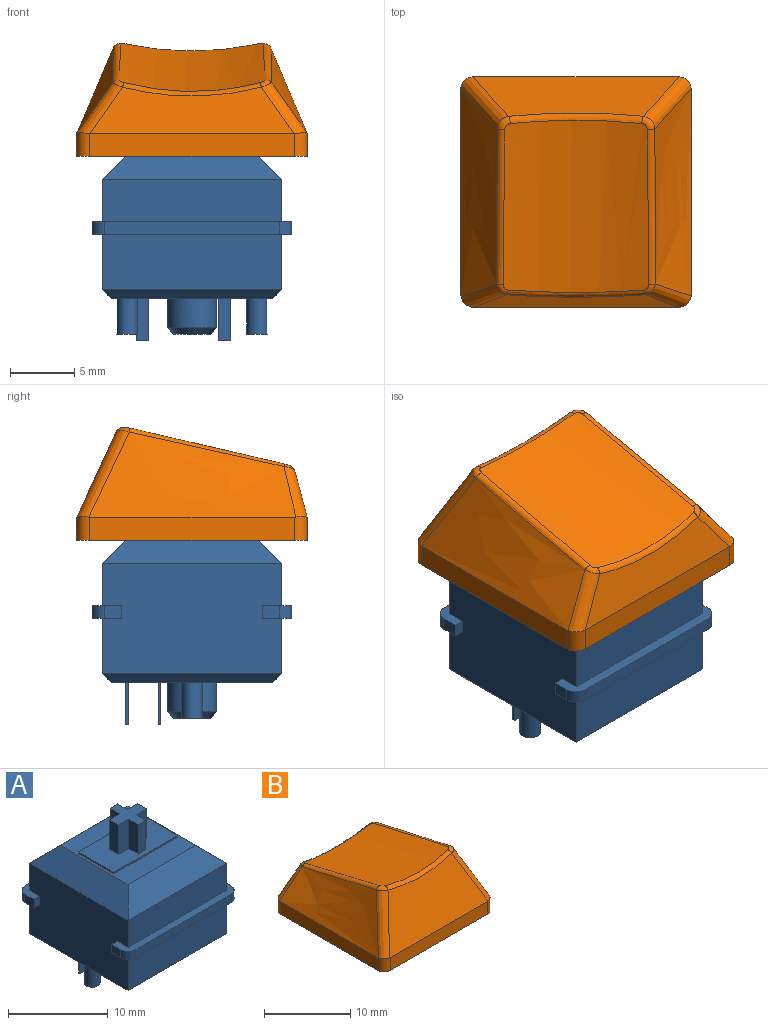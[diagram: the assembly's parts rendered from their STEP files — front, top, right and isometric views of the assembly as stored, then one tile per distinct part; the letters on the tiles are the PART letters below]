
ASSEMBLY  parts=2 mates=1
PART A: 69 faces, bbox 15.6x15.6x18.6 mm
  f0: plane 15.6x2.3mm, normal (0,0,-1), area 14.4mm2, adj f2,f3,f28,f30,f35,f60,f62,f63
  f1: plane 15.6x2.3mm, normal (0,0,-1), area 14.4mm2, adj f28,f30,f33,f34,f36,f59,f61,f64
  f2: plane 1.3x1mm, normal (1,0,0), area 1.3mm2, adj f0,f32,f62,f66
  f3: plane 1.3x1mm, normal (-1,0,0), area 1.3mm2, adj f0,f32,f63,f68
  f4: plane 15.6x2.3mm, normal (0,0,1), area 14.4mm2, adj f28,f30,f31,f33,f34,f36,f61,f64
  f5: plane 14x2.2mm, normal (-0.71,0,0.71), area 36.7mm2, adj f6,f7,f26,f30
  f6: plane 14x2.2mm, normal (0,-0.71,0.71), area 36.7mm2, adj f5,f7,f27,f31
  f7: plane 9.6x9.6mm, normal (0,0,1), area 47.2mm2, adj f5,f6,f8,f9,f10,f11,f26,f27
  f8: plane 5x0.2mm, normal (1,0,0), area 1mm2, adj f7,f9,f11,f12
  f9: plane 9x0.2mm, normal (0,1,0), area 1.8mm2, adj f7,f8,f10,f12
  f10: plane 5x0.2mm, normal (-1,0,0), area 1mm2, adj f7,f9,f11,f12
  f11: plane 9x0.2mm, normal (0,-1,0), area 1.8mm2, adj f7,f8,f10,f12
  f12: plane 9x5mm, normal (0,0,1), area 36.9mm2, adj f8,f9,f10,f11,f13,f14,f15,f16
  f13: plane 3.6x1.35mm, normal (1,0,0), area 4.9mm2, adj f12,f14,f24,f25
  f14: plane 3.6x1.08mm, normal (0,1,0), area 3.9mm2, adj f12,f13,f15,f25
  f15: plane 3.6x1.35mm, normal (-1,0,0), area 4.9mm2, adj f12,f14,f16,f25
  f16: plane 3.6x1.46mm, normal (0,1,0), area 5.3mm2, adj f12,f15,f17,f25
  f17: plane 3.6x1.3mm, normal (-1,0,0), area 4.7mm2, adj f12,f16,f18,f25
  f18: plane 3.6x1.46mm, normal (0,-1,0), area 5.3mm2, adj f12,f17,f19,f25
  f19: plane 3.6x1.35mm, normal (-1,0,0), area 4.9mm2, adj f12,f18,f20,f25
  f20: plane 3.6x1.08mm, normal (0,-1,0), area 3.9mm2, adj f12,f19,f21,f25
  f21: plane 3.6x1.35mm, normal (1,0,0), area 4.9mm2, adj f12,f20,f22,f25
  f22: plane 3.6x1.46mm, normal (0,-1,0), area 5.3mm2, adj f12,f21,f23,f25
  f23: plane 3.6x1.3mm, normal (1,0,0), area 4.7mm2, adj f12,f22,f24,f25
  f24: plane 3.6x1.46mm, normal (0,1,0), area 5.3mm2, adj f12,f13,f23,f25
  f25: plane 4x4mm, normal (0,0,1), area 8.1mm2, adj f13,f14,f15,f16,f17,f18,f19,f20
  f26: plane 14x2.2mm, normal (0,0.71,0.71), area 36.7mm2, adj f5,f7,f27,f29
  f27: plane 14x2.2mm, normal (0.71,0,0.71), area 36.7mm2, adj f6,f7,f26,f28
  f28: plane 14x8.6mm, normal (1,0,0), area 117.4mm2, adj f0,f1,f4,f27,f29,f31,f32,f55
  f29: plane 14x3.3mm, normal (0,1,0), area 46.2mm2, adj f26,f28,f30,f32
  f30: plane 14x8.6mm, normal (-1,0,0), area 117.4mm2, adj f0,f1,f4,f5,f29,f31,f32,f57
  f31: plane 14x3.3mm, normal (0,-1,0), area 46.2mm2, adj f4,f6,f28,f30
  f32: plane 15.6x2.3mm, normal (0,0,1), area 14.4mm2, adj f2,f3,f28,f29,f30,f35,f62,f63
  f33: plane 13.6x1mm, normal (0,-1,0), area 13.6mm2, adj f1,f4,f61,f64
  f34: plane 1.3x1mm, normal (1,0,0), area 1.3mm2, adj f1,f4,f61,f65
  f35: plane 13.6x1mm, normal (0,1,0), area 13.6mm2, adj f0,f32,f62,f63
  f36: plane 1.3x1mm, normal (-1,0,0), area 1.3mm2, adj f1,f4,f64,f67
  f37: plane 2.85x2.85mm, normal (0,0,-1), area 6.4mm2, adj f38
  f38: cone r=1.43mm half-angle=45deg, axis (0,0,1), area 7.4mm2, adj f37,f43
  f39: plane 1x0.2mm, normal (0,0,-1), area 0.2mm2, adj f44,f45,f46,f47
  f40: plane 1x0.2mm, normal (0,0,-1), area 0.2mm2, adj f48,f49,f50,f51
  f41: plane 1.6x1.6mm, normal (0,0,-1), area 2mm2, adj f52
  f42: plane 1.6x1.6mm, normal (0,0,-1), area 2mm2, adj f53
  f43: cylinder r=1.93mm len=3.85mm, axis (0,0,1), area 27.8mm2, adj f38,f54
  f44: plane 3.3x0.2mm, normal (-1,0,0), area 0.7mm2, adj f39,f45,f47,f54
  f45: plane 3.3x1mm, normal (0,1,0), area 3.3mm2, adj f39,f44,f46,f54
  f46: plane 3.3x0.2mm, normal (1,0,0), area 0.7mm2, adj f39,f45,f47,f54
  f47: plane 3.3x1mm, normal (0,-1,0), area 3.3mm2, adj f39,f44,f46,f54
  f48: plane 3.3x0.2mm, normal (-1,0,0), area 0.7mm2, adj f40,f49,f51,f54
  f49: plane 3.3x1mm, normal (0,1,0), area 3.3mm2, adj f40,f48,f50,f54
  f50: plane 3.3x0.2mm, normal (1,0,0), area 0.7mm2, adj f40,f49,f51,f54
  f51: plane 3.3x1mm, normal (0,-1,0), area 3.3mm2, adj f40,f48,f50,f54
  f52: cylinder r=0.8mm len=2.8mm, axis (0,0,1), area 14.1mm2, adj f41,f54
  f53: cylinder r=0.8mm len=2.8mm, axis (0,0,1), area 14.1mm2, adj f42,f54
  f54: plane 12.6x12.6mm, normal (0,0,-1), area 142.7mm2, adj f43,f44,f45,f46,f47,f48,f49,f50
  f55: plane 14x0.7mm, normal (0.71,0,-0.71), area 13.2mm2, adj f28,f54,f56,f58
  f56: plane 14x0.7mm, normal (0,0.71,-0.71), area 13.2mm2, adj f54,f55,f57,f60
  f57: plane 14x0.7mm, normal (-0.71,0,-0.71), area 13.2mm2, adj f30,f54,f56,f58
  f58: plane 14x0.7mm, normal (0,-0.71,-0.71), area 13.2mm2, adj f54,f55,f57,f59
  f59: plane 14x4.3mm, normal (0,-1,0), area 60.2mm2, adj f1,f28,f30,f58
  f60: plane 14x4.3mm, normal (0,1,0), area 60.2mm2, adj f0,f28,f30,f56
  f61: cylinder r=1mm len=1mm, axis (0,0,-1), area 1.6mm2, adj f1,f4,f33,f34
  f62: cylinder r=1mm len=1mm, axis (0,0,1), area 1.6mm2, adj f0,f2,f32,f35
  f63: cylinder r=1mm len=1mm, axis (0,0,-1), area 1.6mm2, adj f0,f3,f32,f35
  f64: cylinder r=1mm len=1mm, axis (0,0,1), area 1.6mm2, adj f1,f4,f33,f36
  f65: plane 1x0.8mm, normal (0,1,0), area 0.8mm2, adj f1,f4,f28,f34
  f66: plane 1x0.8mm, normal (0,-1,0), area 0.8mm2, adj f0,f2,f28,f32
  f67: plane 1x0.8mm, normal (0,1,0), area 0.8mm2, adj f1,f4,f30,f36
  f68: plane 1x0.8mm, normal (0,-1,0), area 0.8mm2, adj f0,f3,f30,f32
PART B: 50 faces, bbox 21.5x21.7x12.5 mm
  f0: plane 18x18mm, normal (0,0,-1), area 67.1mm2, adj f1,f2,f3,f4,f10,f12,f14,f16
  f1: plane 16x1.8mm, normal (1,0,0), area 28.8mm2, adj f0,f8,f10,f16
  f2: plane 16x1.8mm, normal (0,1,0), area 28.8mm2, adj f0,f5,f14,f15,f16,f17
  f3: plane 16x1.8mm, normal (-1,0,0), area 28.8mm2, adj f0,f6,f12,f14
  f4: plane 16x1.8mm, normal (0,-1,0), area 28.8mm2, adj f0,f7,f10,f12
  f5: plane 15.91x3.6mm, normal (0,0.97,0.26), area 44.6mm2, adj f2,f15,f17,f20
  f6: bspline ~18x7.25mm, area 86.5mm2, adj f3,f12,f13,f14,f15,f19
  f7: plane 16.18x6.7mm, normal (0,-0.91,0.42), area 94.1mm2, adj f4,f10,f11,f12,f13,f23
  f8: bspline ~18x7.25mm, area 86.5mm2, adj f1,f10,f11,f16,f17,f24
  f9: cylinder r=22.9mm len=13.49mm, axis (0,0.97,-0.23), area 153.8mm2, adj f18,f19,f20,f21,f22,f23,f24,f25
  f10: cylinder r=1mm len=1.88mm, axis (0,0,-1), area 2.9mm2, adj f0,f1,f4,f7,f8,f11
  f11: bspline ~9.03x5.02mm, area 11.4mm2, adj f7,f8,f10,f25
  f12: cylinder r=1mm len=1.88mm, axis (0,0,1), area 2.9mm2, adj f0,f3,f4,f6,f7,f13
  f13: bspline ~10.12x5.54mm, area 11.4mm2, adj f6,f7,f12,f21
  f14: cylinder r=1mm len=1.81mm, axis (0,0,-1), area 2.8mm2, adj f0,f2,f3,f6,f15
  f15: bspline ~6.35x5.01mm, area 6.5mm2, adj f2,f5,f6,f14,f18
  f16: cylinder r=1mm len=1.81mm, axis (0,0,1), area 2.8mm2, adj f0,f1,f2,f8,f17
  f17: bspline ~6.25x4.94mm, area 6.5mm2, adj f2,f5,f8,f16,f22
  f18: bspline ~1.11x0.93mm, area 0.5mm2, adj f9,f15,f19,f20
  f19: bspline ~17.83x4.37mm, area 8.2mm2, adj f6,f9,f18,f21
  f20: bspline ~10.85x1.04mm, area 5.9mm2, adj f5,f9,f18,f22
  f21: bspline ~1.22x1.15mm, area 0.8mm2, adj f9,f13,f19,f23
  f22: bspline ~1.11x1.06mm, area 0.5mm2, adj f9,f17,f20,f24
  f23: bspline ~10.49x0.83mm, area 7.2mm2, adj f7,f9,f21,f25
  f24: bspline ~17.79x4.36mm, area 8.2mm2, adj f8,f9,f22,f25
  f25: bspline ~1.31x1.07mm, area 0.8mm2, adj f9,f11,f23,f24
  f26: plane 16.1x1.69mm, normal (-1,0,0), area 24.8mm2, adj f0,f27,f29,f33
  f27: plane 16x1.67mm, normal (0,-1,0), area 26.7mm2, adj f0,f26,f28,f30,f31,f33
  f28: plane 16.1x1.69mm, normal (1,0,0), area 24.8mm2, adj f0,f27,f29,f31
  f29: plane 16x1.59mm, normal (0,1,0), area 25.3mm2, adj f0,f26,f28,f32
  f30: plane 16.45x3.93mm, normal (0,-0.97,-0.26), area 39.2mm2, adj f27,f31,f33,f34
  f31: offset ~20x9.25mm, area 77.4mm2, adj f27,f28,f30,f32,f34
  f32: plane 16.26x6.4mm, normal (0,0.91,-0.42), area 86.2mm2, adj f29,f31,f33,f34
  f33: offset ~20x9.25mm, area 77.3mm2, adj f26,f27,f30,f32,f34
  f34: cylinder r=23.9mm len=12.44mm, axis (0,0.97,-0.23), area 115.6mm2, adj f30,f31,f32,f33,f46
  f35: plane 5.13x1.5mm, normal (-1,0,0), area 7.4mm2, adj f36,f44,f45,f49
  f36: plane 5.23x1.51mm, normal (0,-1,0), area 7.8mm2, adj f35,f37,f45,f49
  f37: plane 5.53x1.3mm, normal (-1,0,0), area 7mm2, adj f36,f38,f45,f49
  f38: plane 5.53x1.51mm, normal (0,1,0), area 8.2mm2, adj f37,f39,f45,f49
  f39: plane 5.79x1.5mm, normal (-1,0,0), area 8.4mm2, adj f38,f40,f45,f49
  f40: plane 5.79x1.3mm, normal (0,1,0), area 7.5mm2, adj f39,f41,f45,f49
  f41: plane 5.79x1.5mm, normal (1,0,0), area 8.4mm2, adj f40,f42,f45,f49
  f42: plane 5.53x1.51mm, normal (0,1,0), area 8.2mm2, adj f41,f43,f45,f49
  f43: plane 5.53x1.3mm, normal (1,0,0), area 7mm2, adj f42,f45,f47,f49
  f44: plane 4.79x1.3mm, normal (0,-1,0), area 6.2mm2, adj f35,f45,f48,f49
  f45: plane 5.5x5.5mm, normal (0,0,-1), area 14.3mm2, adj f35,f36,f37,f38,f39,f40,f41,f42
  f46: cylinder r=2.75mm len=5.5mm, axis (0,0,-1), area 94mm2, adj f34,f45
  f47: plane 5.23x1.51mm, normal (0,-1,0), area 7.8mm2, adj f43,f45,f48,f49
  f48: plane 5.13x1.5mm, normal (1,0,0), area 7.4mm2, adj f44,f45,f47,f49
  f49: cylinder r=23.9mm len=4.32mm, axis (0,0.97,-0.23), area 9.8mm2, adj f35,f36,f37,f38,f39,f40,f41,f42
PLACE A at identity fixed
PLACE B rot(axis=(0,0,1),180deg) t=(0,0,11.1)mm
MATE fastened A.f38 <-> B.f46  axis (0,0,1) through (0,0,11.7)mm
